# Revit family: Edelstahlrohrschelle f. Lüftungsrohre V2A, M 8, DN 125-400
name_source: partatom
category: HLS-Bauteile
revit_build: Autodesk Revit 2017 (Build: 20190507_1515(x64)
units: mm (PartAtom-declared; Revit-internal decimal feet)

## family parameters
Arbeitsebenenbasiert = Ja
Beim Laden mit Abzugskörper schneiden = Nein
Bemaßung runder Anschluss = Durchmesser verwenden
Gemeinsam genutzt = Ja
Immer vertikal = Nein
Raumberechnungspunkt = Nein
Teiletyp = Normal

## types (13) — shared parameters
A = 16 mm  [stored 0.0524934 ft]
Anschluss = M8
Anschlußhöhe = 16 mm
Bauart = zweiteilig
Baustoffklasse = B2
DF1 = 20 mm  [stored 0.0656168 ft]
DS = 6 mm  [stored 0.019685 ft]
DVS = 8 mm  [stored 0.0262467 ft]
Dämmstärke = 6 mm  [stored 0.019685 ft]
Fabrikat = MEFA
Farbe Schalldämmeinlage = schwarz
Firma = MEFA Befestigungs- und Montagesysteme GmbH
HGA = 8 mm  [stored 0.0262467 ft]
Kurztext1 = Lüftungsschelle Edelstahl V2A 20x2
MB = 20 mm  [stored 0.0656168 ft]
MD = 2 mm  [stored 0.00656168 ft]
Material = Edelstahl
Material Schalldämmeinlage = TPE
Materialmaße = 20x2 mm
Mengeneinheit = St
Rohraußendurchmesser Zoll = Zoll
Schalldämmeinlage = Gummi
Verschluss = Schraubenverschluss
Vorgabe-Ansicht = 1219 mm
max. Temperaturbeständigkeit = 100 °C
max. zul. Last horizontal = 0.00 kN
max. zul. Last vertikal = 0.00 kN
zero-valued in all types: AB, Stärke Material, max. Rohraußendurchmesser, min. Rohraußendurchmesser

## per-type parameters (varying)
| type | Achsabstand | Artikelnummer | B | D | D0 | DF2 | EAN | Gewicht | Gewicht pro Bauteil | H | Höhe | Kurztext2 | Nennweite DN Rohr | R | RM | Rohraußendurchmesser | S | Verschluss-Schraube | vpe |
| Edelstahlrohrschelle f. Lüftungsrohre, M 8, DN125 | 181 mm | 0468120 | 201 mm | 130 mm  [stored 0.426509 ft] | 142 mm  [stored 0.465879 ft] | 39 mm  [stored 0.127953 ft] | 4250928411884 | 0.23 kg | 0.23 kg | 154 mm  [stored 0.505249 ft] | 154 mm | DN 125 M8 TPE | 125 mm  [stored 0.410105 ft] | 71 mm  [stored 0.23294 ft] | 73 mm  [stored 0.239501 ft] | 129 mm  [stored 0.423228 ft] | 181 mm | M6 | 50 St |
| Edelstahlrohrschelle f. Lüftungsrohre, M 8, DN140 | 196 mm | 0468122 | 216 mm | 145 mm  [stored 0.475722 ft] | 157 mm  [stored 0.515092 ft] | 39 mm  [stored 0.127953 ft] | 4250928411891 | 0.27 kg | 0.27 kg | 169 mm | 169 mm | DN 140 M8 TPE | 140 mm  [stored 0.459318 ft] | 79 mm | 81 mm | 144 mm  [stored 0.472441 ft] | 196 mm | M8 | 50 St |
| Edelstahlrohrschelle f. Lüftungsrohre, M 8, DN150 | 206 mm | 0468123 | 226 mm | 155 mm  [stored 0.50853 ft] | 167 mm | 39 mm  [stored 0.127953 ft] | 4250928411907 | 0.31 kg | 0.31 kg | 179 mm | 179 mm | DN 150 M8 TPE | 150 mm | 84 mm | 86 mm  [stored 0.282152 ft] | 154 mm  [stored 0.505249 ft] | 206 mm | M8 | 50 St |
| Edelstahlrohrschelle f. Lüftungsrohre, M 8, DN 160 | 216 mm | 0468124 | 236 mm | 165 mm | 177 mm | 39 mm  [stored 0.127953 ft] | 4250928411914 | 0.32 kg | 0.32 kg | 189 mm | 189 mm | DN 160 M8 TPE | 160 mm  [stored 0.524934 ft] | 89 mm | 91 mm | 164 mm  [stored 0.538058 ft] | 216 mm | M8 | 50 St |
| Edelstahlrohrschelle f. Lüftungsrohre, M 8, DN180 | 236 mm | 0468127 | 256 mm | 185 mm | 197 mm | 39 mm  [stored 0.127953 ft] | 4250928411921 | 0.36 kg | 0.36 kg | 209 mm | 209 mm | DN 180 M8 TPE | 180 mm | 99 mm | 101 mm | 184 mm | 236 mm | M8 | 1 St |
| Edelstahlrohrschelle f. Lüftungsrohre, M 8, DN200 | 258 mm | 0468129 | 278 mm | 205 mm | 217 mm | 41 mm  [stored 0.134514 ft] | 4250928411938 | 0.39 kg | 0.39 kg | 229 mm | 229 mm | DN 200 M8 TPE | 200 mm | 109 mm | 111 mm | 204 mm | 258 mm | M8 | 1 St |
| Edelstahlrohrschelle f. Lüftungsrohre, M 8, DN224 | 282 mm | 0468132 | 302 mm | 229 mm | 241 mm | 41 mm  [stored 0.134514 ft] | 4250928411945 | 0.42 kg | 0.42 kg | 253 mm | 253 mm | DN 224 M8 TPE | 224 mm | 121 mm | 123 mm | 228 mm | 282 mm | M8 | 1 St |
| Edelstahlrohrschelle f. Lüftungsrohre, M 8, DN250 | 308 mm | 0468135 | 328 mm | 255 mm | 267 mm | 41 mm  [stored 0.134514 ft] | 4250928411952 | 0.46 kg | 0.46 kg | 279 mm | 279 mm | DN 250 M8 TPE | 250 mm | 134 mm | 136 mm  [stored 0.446194 ft] | 254 mm | 308 mm | M8 | 1 St |
| Edelstahlrohrschelle f. Lüftungsrohre, M 8, DN280 | 338 mm | 0468140 | 358 mm | 285 mm | 297 mm | 41 mm  [stored 0.134514 ft] | 4250928411969 | 0.50 kg | 0.50 kg | 309 mm | 309 mm | DN 280 M8 TPE | 280 mm | 149 mm | 151 mm | 284 mm | 338 mm | M8 | 1 St |
| Edelstahlrohrschelle f. Lüftungsrohre, M 8, DN300 | 360 mm | 0468143 | 380 mm | 307 mm | 319 mm | 41 mm  [stored 0.134514 ft] | 4250928411976 | 0.51 kg | 0.51 kg | 331 mm | 331 mm | DN 300 M8 TPE | 300 mm | 160 mm  [stored 0.524934 ft] | 162 mm | 305 mm | 360 mm | M8 | 1 St |
| Edelstahlrohrschelle f. Lüftungsrohre, M 8, DN315 | 375 mm | 0468146 | 395 mm | 322 mm | 334 mm | 41 mm  [stored 0.134514 ft] | 4250928411983 | 0.56 kg | 0.56 kg | 346 mm | 346 mm | DN 315 M8 TPE | 315 mm | 167 mm | 169 mm | 320 mm | 375 mm | M8 | 1 St |
| Edelstahlrohrschelle f. Lüftungsrohre, M 8, DN355 | 415 mm | 0468152 | 435 mm | 362 mm | 374 mm | 41 mm  [stored 0.134514 ft] | 4250928411990 | 0.61 kg | 0.61 kg | 386 mm | 386 mm | DN 355 M8 TPE | 355 mm | 187 mm | 189 mm | 360 mm | 415 mm | M8 | 1 St |
| Edelstahlrohrschelle f. Lüftungsrohre, M 8, DN400 | 462 mm | 0468156 | 480 mm | 407 mm | 419 mm | 41 mm  [stored 0.134514 ft] | 4250928412003 | 0.68 kg | 0.68 kg | 431 mm | 431 mm | DN 400 M8 TPE | 400 mm | 210 mm | 212 mm | 405 mm | 460 mm | M8 | 1 St |

note: [stored X ft] marks values corroborated as IEEE doubles in the binary element streams (Revit-internal decimal feet)

## geometry (parser evidence)
native form markers: Sweep x8
no freeform markers — native parametric forms only
